# Revit family: Z181-M1
name_source: partatom
category: Aparatos sanitarios
units: mm (PartAtom-declared; Revit-internal decimal feet)

## family parameters
Compartido = No
Corte con vacíos al cargar = No
Cota de conector redondo = Diámetro de uso
Número OmniClass = 23.45.55.14
Punto de cálculo de habitación = No
Se basa en plano de trabajo = No
Siempre vertical = Sí
Tipo de pieza = Normal
Título OmniClass = Single Faucets

## types (1)
- Z181-M1
    Code = Z181-M1
    Collection = Jana
    Código de montaje = D2020300
    Descripción = Single handle lavatory set
    Elevación por defecto = 0 mm  [stored 0 ft]
    FV- Material = FV- Cromado
    Fabricante = FV
    Installation guide = https://fv-internacional.com
    Spec. Sheet = https://fv-internacional.com
    URL = https://fv-internacional.com

note: [stored X ft] marks values corroborated as IEEE doubles in the binary element streams (Revit-internal decimal feet)

## geometry (parser evidence)
native form markers: Sweep x3
no freeform markers — native parametric forms only
